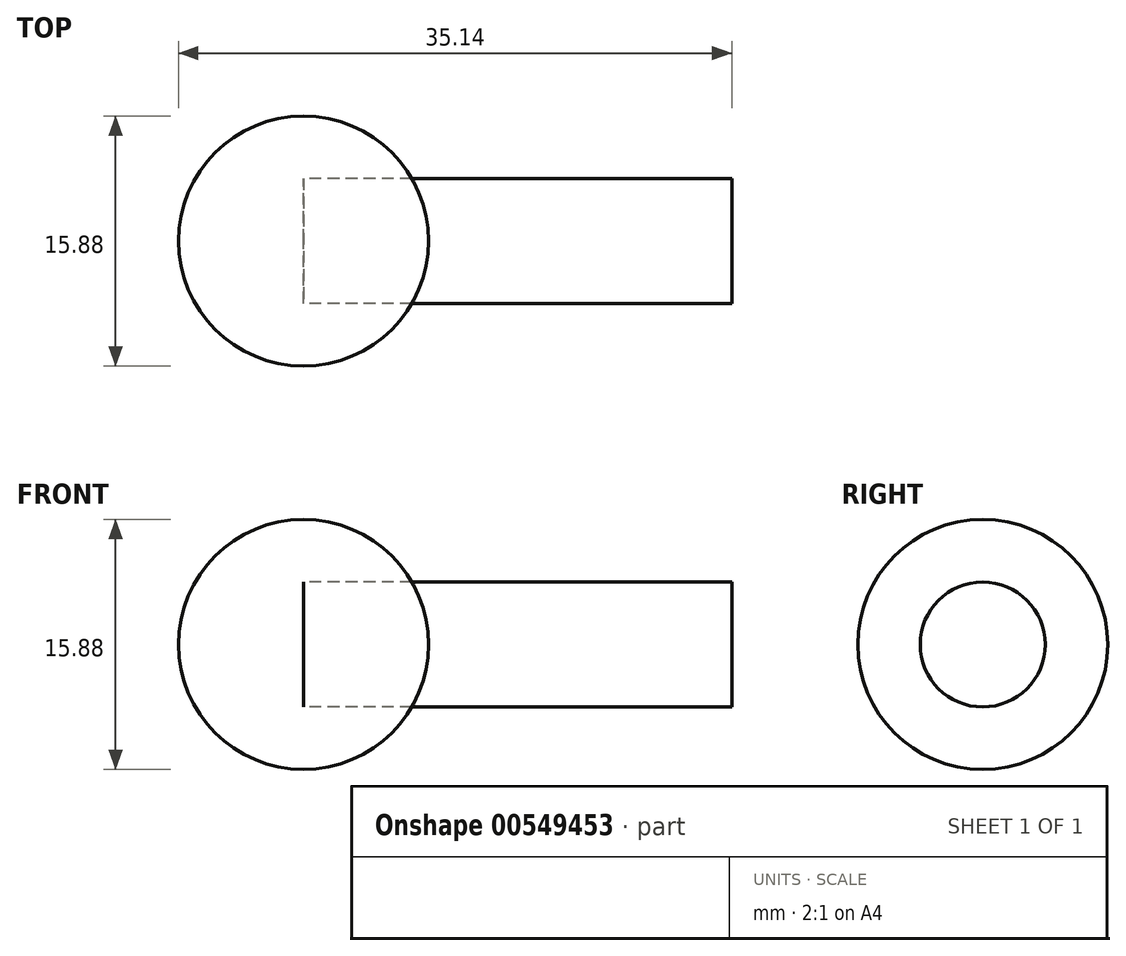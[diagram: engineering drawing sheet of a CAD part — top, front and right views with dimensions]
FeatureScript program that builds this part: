
annotation { "Feature Type Name" : "Feature", "Feature Type Description" : "" }
export const myFeature = defineFeature(function(context is Context, id is Id, definition is map)
    precondition{}
    {
        {
            var Q0;
            Q0=qCreatedBy(makeId("Right.planeOp"),FACE);
            var sketch = newSketch(context, id + "F0", { "sketchPlane" : qUnion([Q0])});
            skArc(sketch, "E0", {"start": v(0, 7.94) * mm, "mid": v(-7.94, 0) * mm, "end": v(0, -7.94) * mm});
            skLineSegment(sketch, "E1", {"start": v(0, 7.94) * mm, "end": v(0, -7.94) * mm, "construction": true});
            skLineSegment(sketch, "E2", {"start": v(0, 7.94) * mm, "end": v(0, -7.94) * mm});
            skSolve(sketch);
        }
        {
            var Q0;
            Q0 = qSketchRegion(id + "F0", true);
            var Q1;
            Q1=sQuery(id+"F0.wireOp",EDGE,"E2");
            revolve(context, id + "F1", {"entities" : qUnion([Q0]), "axis" : qUnion([Q1]), "revolveType" : RevolveType.FULL});
        }
        {
            var Q0;
            Q0=makeQuery(id+"F0.imprint","IMPRINT",FACE,{"disambiguationData":[TD([[makeQuery(id+"F0.imprint","IMPRINT",EDGE,{"derivedFrom":sQuery(id+"F0.wireOp",EDGE,"E0")}),1.0]])]});
            var sketch = newSketch(context, id + "F2", { "sketchPlane" : qUnion([Q0])});
            skCircle(sketch, "E3", {"center": v(0, 0) * mm, "radius": 3.97 * mm});
            skSolve(sketch);
        }
        {
            var Q0;
            {var subQ0=sQuery(id+"F2.wireOp",EDGE,"E3");var subQ1=makeQuery(id+"F0.imprint","IMPRINT",EDGE,{"derivedFrom":sQuery(id+"F0.wireOp",EDGE,"E2")});var subQ2=makeQuery(id+"F2.imprint","INTERSECT",VERTEX,{"disambiguationData":[OD(0.0)],"derivedFrom":[subQ1,subQ0]});Q0=makeQuery(id+"F2.imprint","IMPRINT",FACE,{"disambiguationData":[TD([[makeQuery(id+"F2.imprint","IMPRINT",EDGE,{"disambiguationData":[TD([[subQ2,-1.0]])],"derivedFrom":subQ0}),1.0]])]});}
            var Q1;
            {var subQ0=sQuery(id+"F2.wireOp",EDGE,"E3");var subQ1=makeQuery(id+"F0.imprint","IMPRINT",EDGE,{"derivedFrom":sQuery(id+"F0.wireOp",EDGE,"E2")});var subQ2=makeQuery(id+"F2.imprint","INTERSECT",VERTEX,{"disambiguationData":[OD(0.0)],"derivedFrom":[subQ1,subQ0]});Q1=makeQuery(id+"F2.imprint","IMPRINT",FACE,{"disambiguationData":[TD([[makeQuery(id+"F2.imprint","IMPRINT",EDGE,{"disambiguationData":[TD([[subQ2,1.0]])],"derivedFrom":subQ0}),1.0]])]});}
            extrude(context, id + "F3", {"entities" : qUnion([Q0, Q1]), "depth" : 27.2 * mm, "offsetDistance" : 25.4 * mm});
        }
    });
